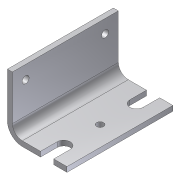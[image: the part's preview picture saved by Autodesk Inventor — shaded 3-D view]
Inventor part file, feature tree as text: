
AUTODESK INVENTOR PART (.ipt)
format: ipt  version: 2012 (Build 160160000, 160)  size: 119,808 bytes
history: native  units: in
note: dims shown in document units (in); Inventor stores cm internally (conversion verified against a paired STEP export)
features: extrude x2, hole x2, sketch x2
ambient origin geometry x8: Origin, YZ Plane, XZ Plane, XY Plane, X Axis, Y Axis, Z Axis, Center Point
bodies: Solid1 (feature_tree)
feature tree (6):
  extrude  "Extrusion1"  Depth=0.375in
  hole  "Hole1"  [1 undecoded]
  hole  "Hole2"  [1 undecoded]
  extrude  "Extrusion2"  Depth=0.5in
  sketch  "Sketch1"  dims[d0=0.188in d1=0.375in]
  sketch  "Sketch2"  dims[d2=0.563in d3=2.25in d4=4.0in d5=0.0in d6=0.5in d7=0.5in d8=0.265in d9=0.75in d10=0.375in d11=0.25in d12=0.5635in d13=1.0in d14=0.8108in d15=0.5in d16=0.5in d17=0.265in d18=0.75in d19=0.375in d20=0.25in d21=0.5635in d22=1.0in d23=0.8108in d24=0.5in d25=0.75in d26=0.625in d27=0.265in d28=2.0in d29=0.75in d30=4.0in d31=0.0in]
note: 2 required parameter values undecoded (feature->parameter linkage not recoverable at this tier; creation-order binding heuristic only, values carry confidence <= 0.55)
